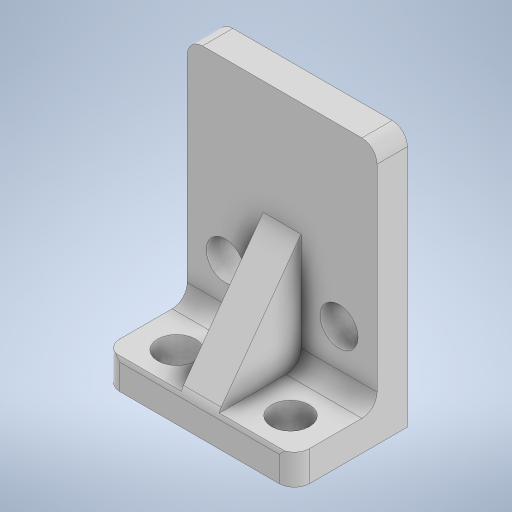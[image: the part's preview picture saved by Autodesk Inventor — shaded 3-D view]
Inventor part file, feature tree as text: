
AUTODESK INVENTOR PART (.ipt)
format: ipt  version: 2024.3 (Build 283343000, 343)  size: 305,664 bytes
history: native  units: mm
features: sketch x7, extrude x5, hole x2, other x1, fillet x1, projected_geometry x1
ambient origin geometry x8: Origin, YZ Plane, XZ Plane, XY Plane, X Axis, Y Axis, Z Axis, Center Point
bodies: Body1 (feature_tree)
feature tree (17):
  other  "ソリッド1"
  extrude  "押し出し1"  Depth=4.0mm
  extrude  "押し出し2"  Depth=25.0mm
  hole  "穴1"  [1 undecoded]
  hole  "穴2"  [1 undecoded]
  extrude  "押し出し5"  Depth=30.0mm TaperAngle=0.0deg
  extrude  "押し出し6"  Depth=15.0mm
  fillet  "フィレット1"  Radius=6.4mm
  extrude  "押し出し7"  Depth=6.4mm
  sketch  "スケッチ1"
  sketch  "スケッチ2"
  sketch  "スケッチ3"
  sketch  "スケッチ4"
  sketch  "スケッチ7"
  sketch  "スケッチ8"
  projected_geometry  "投影ループ3"
  sketch  "スケッチ9"
note: 2 required parameter values undecoded (feature->parameter linkage not recoverable at this tier; creation-order binding heuristic only, values carry confidence <= 0.55)
